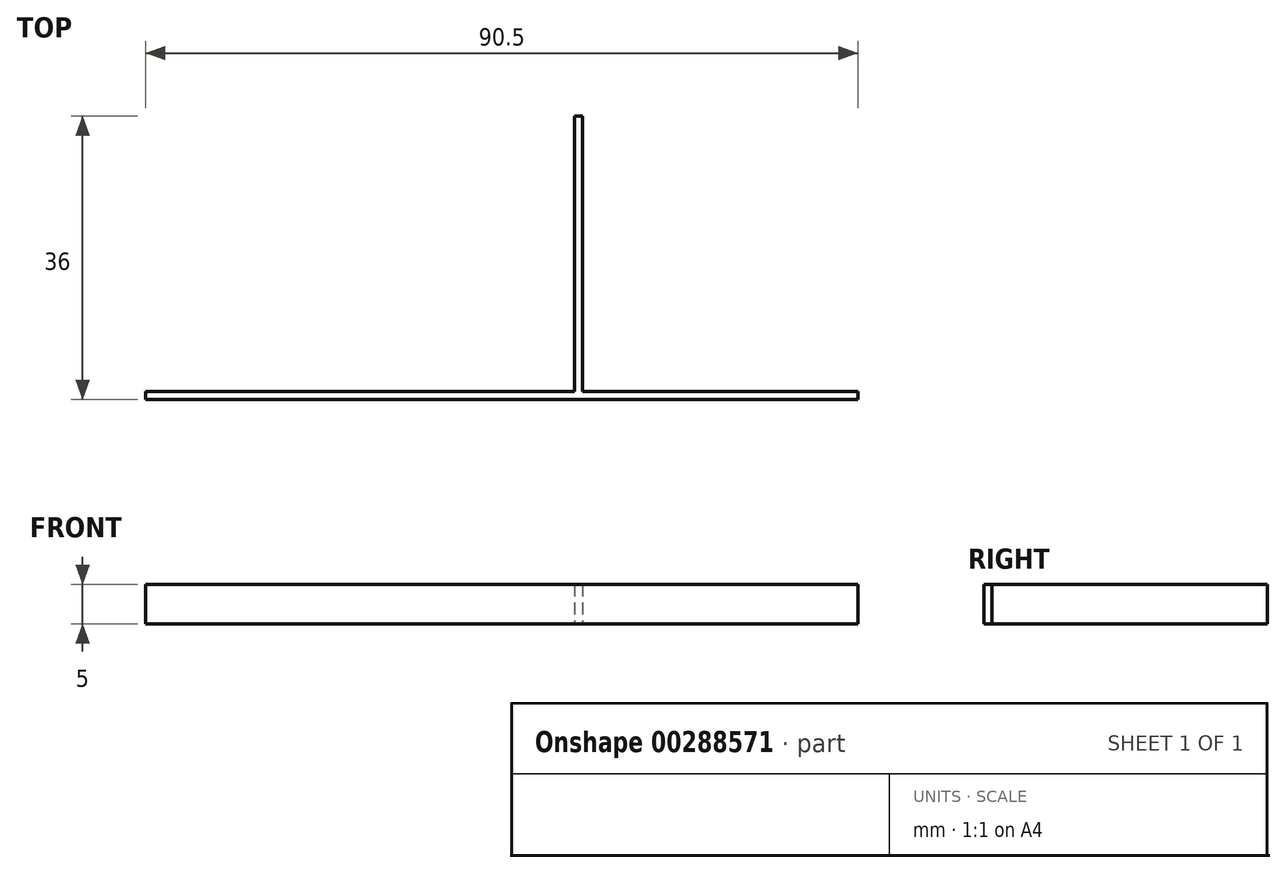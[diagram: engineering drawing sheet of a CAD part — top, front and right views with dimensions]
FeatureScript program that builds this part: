
annotation { "Feature Type Name" : "Feature", "Feature Type Description" : "" }
export const myFeature = defineFeature(function(context is Context, id is Id, definition is map)
    precondition{}
    {
        {
            var Q0;
            Q0=qCreatedBy(makeId("Top.planeOp"),FACE);
            var sketch = newSketch(context, id + "F0", { "sketchPlane" : qUnion([Q0])});
            skLineSegment(sketch, "E0.bottom", {"start": v(0, 0) * mm, "end": v(-45.25, 0) * mm});
            skLineSegment(sketch, "E0.top", {"start": v(0, 1) * mm, "end": v(-45.25, 1) * mm});
            skLineSegment(sketch, "E0.left", {"start": v(0, 0) * mm, "end": v(0, 1) * mm});
            skLineSegment(sketch, "E0.right", {"start": v(-45.25, 0) * mm, "end": v(-45.25, 1) * mm});
            skLineSegment(sketch, "E1.bottom", {"start": v(-10.25, 1) * mm, "end": v(-9.25, 1) * mm});
            skLineSegment(sketch, "E1.top", {"start": v(-10.25, 36) * mm, "end": v(-9.25, 36) * mm});
            skLineSegment(sketch, "E1.left", {"start": v(-10.25, 1) * mm, "end": v(-10.25, 36) * mm});
            skLineSegment(sketch, "E1.right", {"start": v(-9.25, 1) * mm, "end": v(-9.25, 36) * mm});
            skLineSegment(sketch, "E2.MirrorCS", {"start": v(10.25, 36) * mm, "end": v(9.25, 36) * mm});
            skLineSegment(sketch, "E3.MirrorCS", {"start": v(9.25, 1) * mm, "end": v(9.25, 36) * mm});
            skLineSegment(sketch, "E4.MirrorCS", {"start": v(10.25, 1) * mm, "end": v(10.25, 36) * mm});
            skLineSegment(sketch, "E5.MirrorCS", {"start": v(10.25, 1) * mm, "end": v(9.25, 1) * mm});
            skLineSegment(sketch, "E6.MirrorCS", {"start": v(0, 1) * mm, "end": v(45.25, 1) * mm});
            skLineSegment(sketch, "E7.MirrorCS", {"start": v(0, 0) * mm, "end": v(45.25, 0) * mm});
            skLineSegment(sketch, "E8.MirrorCS", {"start": v(45.25, 0) * mm, "end": v(45.25, 1) * mm});
            skSolve(sketch);
        }
        {
            var Q0;
            Q0=makeQuery(id+"F0.imprint","IMPRINT",FACE,{"disambiguationData":[TD([[makeQuery(id+"F0.imprint","IMPRINT",EDGE,{"derivedFrom":sQuery(id+"F0.wireOp",EDGE,"E1.bottom")}),1.0]])]});
            var Q1;
            Q1=makeQuery(id+"F0.imprint","IMPRINT",FACE,{"disambiguationData":[TD([[makeQuery(id+"F0.imprint","IMPRINT",EDGE,{"derivedFrom":sQuery(id+"F0.wireOp",EDGE,"E2.MirrorCS")}),1.0]])]});
            var Q2;
            {var subQ3=sQuery(id+"F0.wireOp",EDGE,"E0.left");Q2=makeQuery(id+"F0.imprint","IMPRINT",FACE,{"disambiguationData":[TD([[makeQuery(id+"F0.imprint","IMPRINT",EDGE,{"derivedFrom":subQ3}),-1.0]])]});}
            var Q3;
            Q3=makeQuery(id+"F0.imprint","IMPRINT",FACE,{"disambiguationData":[TD([[makeQuery(id+"F0.imprint","IMPRINT",EDGE,{"derivedFrom":sQuery(id+"F0.wireOp",EDGE,"E0.bottom")}),-1.0]])]});
            extrude(context, id + "F1", {"entities" : qUnion([Q0, Q1, Q2, Q3]), "endBound" : BoundingType.SYMMETRIC, "depth" : 5 * mm});
        }
    });
